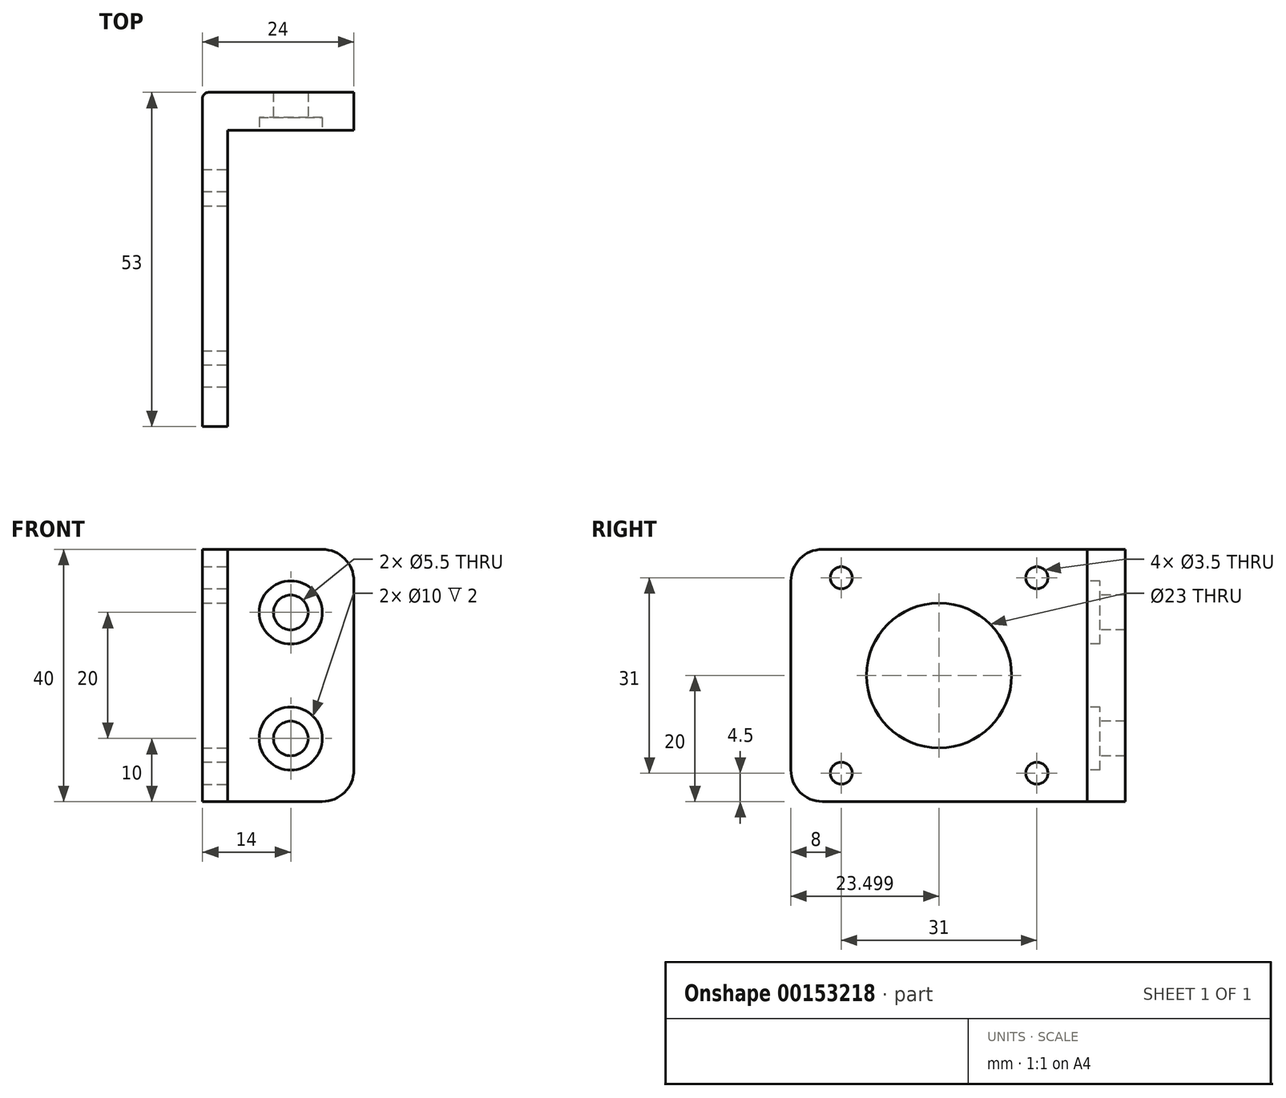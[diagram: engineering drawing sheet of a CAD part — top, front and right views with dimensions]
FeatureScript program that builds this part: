
annotation { "Feature Type Name" : "Feature", "Feature Type Description" : "" }
export const myFeature = defineFeature(function(context is Context, id is Id, definition is map)
    precondition{}
    {
        {
            var Q0;
            Q0=qCreatedBy(makeId("Top.planeOp"),FACE);
            var sketch = newSketch(context, id + "F0", { "sketchPlane" : qUnion([Q0])});
            skLineSegment(sketch, "E0", {"start": v(0, -29.61) * mm, "end": v(0, 23.39) * mm});
            skLineSegment(sketch, "E1", {"start": v(0, 23.39) * mm, "end": v(24, 23.39) * mm});
            skLineSegment(sketch, "E2", {"start": v(24, 23.39) * mm, "end": v(24, 17.39) * mm});
            skLineSegment(sketch, "E3", {"start": v(4, 17.39) * mm, "end": v(4, -29.61) * mm});
            skLineSegment(sketch, "E4", {"start": v(4, -29.61) * mm, "end": v(0, -29.61) * mm});
            skLineSegment(sketch, "E5", {"start": v(4, 17.39) * mm, "end": v(24, 17.39) * mm});
            skSolve(sketch);
        }
        {
            var Q0;
            Q0=makeQuery(id+"F0.imprint","IMPRINT",FACE,{"disambiguationData":[TD([[makeQuery(id+"F0.imprint","IMPRINT",EDGE,{"derivedFrom":sQuery(id+"F0.wireOp",EDGE,"E0")}),-1.0]])]});
            extrude(context, id + "F5", {"entities" : qUnion([Q0]), "depth" : 40 * mm});
        }
        {
            var Q0;
            Q0=makeQuery(id+"F5.opExtrude","SWEPT_FACE",FACE,{"disambiguationData":[OSD([sQuery(id+"F0.wireOp",EDGE,"E3")])]});
            var sketch = newSketch(context, id + "F6", { "sketchPlane" : qUnion([Q0])});
            skPoint(sketch, "E6", {"position": v(-6.11, 20) * mm});
            skPoint(sketch, "E6.positionSnap0", {"position": v(-6.11, 40) * mm});
            skPoint(sketch, "E6.positionSnap1", {"position": v(-29.61, 20) * mm});
            skLineSegment(sketch, "E7.bottom", {"start": v(9.39, 4.5) * mm, "end": v(-21.61, 4.5) * mm});
            skLineSegment(sketch, "E7.top", {"start": v(9.39, 35.5) * mm, "end": v(-21.61, 35.5) * mm});
            skLineSegment(sketch, "E7.left", {"start": v(9.39, 4.5) * mm, "end": v(9.39, 35.5) * mm});
            skLineSegment(sketch, "E7.right", {"start": v(-21.61, 4.5) * mm, "end": v(-21.61, 35.5) * mm});
            skSolve(sketch);
        }
        {
            var Q0;
            Q0=sQuery(id+"F6.wireOp",VERTEX,"E7.top.end");
            var Q1;
            Q1=sQuery(id+"F6.wireOp",VERTEX,"E7.top.start");
            var Q2;
            Q2=sQuery(id+"F6.wireOp",VERTEX,"E7.right.start");
            var Q3;
            Q3=sQuery(id+"F6.wireOp",VERTEX,"E7.bottom.start");
            var Q4;
            Q4=makeQuery(id+"F5.opExtrude","SWEPT_BODY",BODY,{"disambiguationData":[OSD([sQuery(id+"F0.wireOp",EDGE,"E0"),sQuery(id+"F0.wireOp",EDGE,"E1"),sQuery(id+"F0.wireOp",EDGE,"E2"),sQuery(id+"F0.wireOp",EDGE,"E3"),sQuery(id+"F0.wireOp",EDGE,"E4"),sQuery(id+"F0.wireOp",EDGE,"E5")])]});
            hole(context, id + "F1", {"style" : HoleStyle.SIMPLE, "endStyle" : HoleEndStyle.THROUGH, "holeDiameter" : 3.5 * mm, "locations" : qUnion([Q0, Q1, Q2, Q3]), "scope" : qUnion([Q4]), "isTappedThrough" : true});
        }
        {
            var Q0;
            Q0=sQuery(id+"F6.wireOp",VERTEX,"E6");
            var Q1;
            Q1=makeQuery(id+"F5.opExtrude","SWEPT_BODY",BODY,{"disambiguationData":[OSD([sQuery(id+"F0.wireOp",EDGE,"E0"),sQuery(id+"F0.wireOp",EDGE,"E1"),sQuery(id+"F0.wireOp",EDGE,"E2"),sQuery(id+"F0.wireOp",EDGE,"E3"),sQuery(id+"F0.wireOp",EDGE,"E4"),sQuery(id+"F0.wireOp",EDGE,"E5")])]});
            hole(context, id + "F7", {"style" : HoleStyle.SIMPLE, "endStyle" : HoleEndStyle.THROUGH, "holeDiameter" : 23 * mm, "locations" : qUnion([Q0]), "scope" : qUnion([Q1]), "isTappedThrough" : true});
        }
        {
            var Q0;
            Q0=makeQuery(id+"F5.opExtrude","SWEPT_FACE",FACE,{"disambiguationData":[OSD([sQuery(id+"F0.wireOp",EDGE,"E5")])]});
            var sketch = newSketch(context, id + "F8", { "sketchPlane" : qUnion([Q0])});
            skPoint(sketch, "E8", {"position": v(14, 30) * mm});
            skPoint(sketch, "E8.positionSnap0", {"position": v(14, 40) * mm});
            skPoint(sketch, "E9", {"position": v(14, 10) * mm});
            skSolve(sketch);
        }
        {
            var Q0;
            Q0=sQuery(id+"F8.wireOp",VERTEX,"E8");
            var Q1;
            Q1=sQuery(id+"F8.wireOp",VERTEX,"E9");
            var Q2;
            Q2=makeQuery(id+"F5.opExtrude","SWEPT_BODY",BODY,{"disambiguationData":[OSD([sQuery(id+"F0.wireOp",EDGE,"E0"),sQuery(id+"F0.wireOp",EDGE,"E1"),sQuery(id+"F0.wireOp",EDGE,"E2"),sQuery(id+"F0.wireOp",EDGE,"E3"),sQuery(id+"F0.wireOp",EDGE,"E4"),sQuery(id+"F0.wireOp",EDGE,"E5")])]});
            hole(context, id + "F2", {"style" : HoleStyle.C_BORE, "endStyle" : HoleEndStyle.THROUGH, "holeDiameter" : 5.5 * mm, "cBoreDiameter" : 10 * mm, "cBoreDepth" : 2 * mm, "locations" : qUnion([Q0, Q1]), "scope" : qUnion([Q2]), "isTappedThrough" : true});
        }
        {
            var Q0;
            Q0=makeQuery(id+"F5.opExtrude","CAP_EDGE",EDGE,{"disambiguationData":[OSD([sQuery(id+"F0.wireOp",EDGE,"E4")])],"isStart":false});
            var Q1;
            Q1=makeQuery(id+"F5.opExtrude","CAP_EDGE",EDGE,{"disambiguationData":[OSD([sQuery(id+"F0.wireOp",EDGE,"E4")])],"isStart":true});
            var Q2;
            Q2=makeQuery(id+"F5.opExtrude","CAP_EDGE",EDGE,{"disambiguationData":[OSD([sQuery(id+"F0.wireOp",EDGE,"E2")])],"isStart":false});
            var Q3;
            Q3=makeQuery(id+"F5.opExtrude","CAP_EDGE",EDGE,{"disambiguationData":[OSD([sQuery(id+"F0.wireOp",EDGE,"E2")])],"isStart":true});
            fillet(context, id + "F3", {"entities" : qUnion([Q0, Q1, Q2, Q3]), "radius" : 5 * mm, "tangentPropagation" : true, "allowEdgeOverflow" : false});
        }
        {
            var Q0;
            Q0=makeQuery(id+"F5.opExtrude","SWEPT_EDGE",EDGE,{"disambiguationData":[OSD([sQuery(id+"F0.wireOp",EDGE,"E0"),sQuery(id+"F0.wireOp",EDGE,"E1")])]});
            fillet(context, id + "F4", {"entities" : qUnion([Q0]), "radius" : 1 * mm, "tangentPropagation" : true, "allowEdgeOverflow" : false});
        }
    });
